# Revit family: KEUCO_34983010037
name_source: partatom
category: Allgemeines Modell
revit_build: Autodesk Revit 2016 (Build: 20150220_1215(x64)
units: mm (PartAtom-declared; Revit-internal decimal feet)

## family parameters
Arbeitsebenenbasiert = Ja
Beim Laden mit Abzugskörper schneiden = Nein
Bemaßung runder Anschluss = Durchmesser verwenden
Gemeinsam genutzt = Nein
Immer vertikal = Nein
Kann Basisbauteil für Bewehrung sein = Nein
Raumberechnungspunkt = Nein
Teiletyp = Normal

## types (6) — shared parameters
Beschreibung = zur Wandmontage
Softsitz nach oben klappbar
Gewicht = 0.522
Hersteller = KEUCO
Kategorie = ACC
Länge = 450 mm  [stored 1.47638 ft]
Serie = Plan
Tiefe = 537 mm  [stored 1.76181 ft]
URL = https://www.keuco.com
Verwendung = CA / DU
Vorgabe-Ansicht = 1219 mm

## per-type parameters (varying)
| type | Ausschreibungstext | Material Regal | Rahmen Material |
| 34983010037 | KEUCO PLAN CARE Klappsitz 34983010037
schwarzgrauer (RAL 7021) Klappsitz 
aus Polyurethan-Schaum, zur Wandmontage 
in ästhetischem, funktionalem Design, 
für sicheres Sitzen im Duschbereich,
Wandhalter und Sitzträger als Design-Element hochglanzverchromt,
antistatisch, leichte Reinigung ,
kann mit max. 60%-igen Ethanol- 
oder Propanol-Lösungen desinfiziert werden, 
andere Desinfektionsmittel empfehlen sich nicht,
nach oben klappbarer Sitz belastbar bis 150 kg,
Breite 450 mm, Länge der Sitzfläche 500 mm,
Ausladung 537 mm,
Der Sitz wird verdeckt angebracht 

Das Befestigungsmaterial ist separat zu bestellen!

Zur Montage (je nach Ankergrund/Mauerwerk) 
unbedingt erforderlich:
3 x Befestigungs-Set 3 (Artikel-Nr. 34992000100)
oder
3 x Befestigungs-Set 6 (Artikel-Nr. 34992000200)
oder
3 x Befestigungs-Set 9 (Artikel-Nr. 34995000200)
oder
3 x Befestigungs-Set 11 (Artikel-Nr. 34997000100) | Schwarzgrau | Stahl, verchromt |
| 34983010038 | KEUCO PLAN CARE Klappsitz 34983010038
lichtgrauer (RAL 7035) Klappsitz 
aus Polyurethan-Schaum, zur Wandmontage 
in ästhetischem, funktionalem Design, 
für sicheres Sitzen im Duschbereich,
Wandhalter und Sitzträger als Design-Element hochglanzverchromt,
antistatisch, leichte Reinigung ,
kann mit max. 60%-igen Ethanol- 
oder Propanol-Lösungen desinfiziert werden, 
andere Desinfektionsmittel empfehlen sich nicht,
nach oben klappbarer Sitz belastbar bis 150 kg,
Breite 450 mm, Länge der Sitzfläche 500 mm,
Ausladung 537 mm,
Der Sitz wird verdeckt angebracht 

Das Befestigungsmaterial ist separat zu bestellen!

Zur Montage (je nach Ankergrund/Mauerwerk) 
unbedingt erforderlich:
3 x Befestigungs-Set 3 (Artikel-Nr. 34992000100)
oder
3 x Befestigungs-Set 6 (Artikel-Nr. 34992000200)
oder
3 x Befestigungs-Set 9 (Artikel-Nr. 34995000200)
oder
3 x Befestigungs-Set 11 (Artikel-Nr. 34997000100) | Weiß (RAL 9010) | Stahl, verchromt |
| 34983010051 | KEUCO PLAN CARE Klappsitz 34983010051
weißer (RAL 9010) Klappsitz 
aus Polyurethan-Schaum, zur Wandmontage 
in ästhetischem, funktionalem Design, 
für sicheres Sitzen im Duschbereich,
Wandhalter und Sitzträger als Design-Element hochglanzverchromt,
antistatisch, leichte Reinigung ,
kann mit max. 60%-igen Ethanol- 
oder Propanol-Lösungen desinfiziert werden, 
andere Desinfektionsmittel empfehlen sich nicht,
nach oben klappbarer Sitz belastbar bis 150 kg,
Breite 450 mm, Länge der Sitzfläche 500 mm,
Ausladung 537 mm,
Der Sitz wird verdeckt angebracht 

Das Befestigungsmaterial ist separat zu bestellen!

Zur Montage (je nach Ankergrund/Mauerwerk) 
unbedingt erforderlich:
3 x Befestigungs-Set 3 (Artikel-Nr. 34992000100)
oder
3 x Befestigungs-Set 6 (Artikel-Nr. 34992000200)
oder
3 x Befestigungs-Set 9 (Artikel-Nr. 34995000200)
oder
3 x Befestigungs-Set 11 (Artikel-Nr. 34997000100) | Weiß (RAL 9010) | Stahl, verchromt |
| 34983170037 | KEUCO PLAN CARE Klappsitz 34983170037
schwarzgrauer (RAL 7021) Klappsitz 
aus Polyurethan-Schaum, zur Wandmontage 
in ästhetischem, funktionalem Design, 
für sicheres Sitzen im Duschbereich,
Wandhalter und Sitzträger als Design-Element 
aus lackiertem Aluminium,
antistatisch, leichte Reinigung ,
kann mit max. 60%-igen Ethanol- 
oder Propanol-Lösungen desinfiziert werden, 
andere Desinfektionsmittel empfehlen sich nicht,
nach oben klappbarer Sitz belastbar bis 150 kg,
Breite 450 mm, Länge der Sitzfläche 500 mm,
Ausladung 537 mm,
Der Sitz wird verdeckt angebracht 

Das Befestigungsmaterial ist separat zu bestellen!

Zur Montage (je nach Ankergrund/Mauerwerk) 
unbedingt erforderlich:
3 x Befestigungs-Set 3 (Artikel-Nr. 34992000100)
oder
3 x Befestigungs-Set 6 (Artikel-Nr. 34992000200)
oder
3 x Befestigungs-Set 9 (Artikel-Nr. 34995000200)
oder
3 x Befestigungs-Set 11 (Artikel-Nr. 34997000100) | Schwarzgrau | Aluminium 1100-H18 |
| 34983170038 | KEUCO PLAN CARE Klappsitz 34983170038
lichtgrauer (RAL 7035) Klappsitz 
aus Polyurethan-Schaum, zur Wandmontage 
in ästhetischem, funktionalem Design, 
für sicheres Sitzen im Duschbereich,
Wandhalter und Sitzträger als Design-Element 
aus lackiertem Aluminium,
antistatisch, leichte Reinigung ,
kann mit max. 60%-igen Ethanol- 
oder Propanol-Lösungen desinfiziert werden, 
andere Desinfektionsmittel empfehlen sich nicht,
nach oben klappbarer Sitz belastbar bis 150 kg,
Breite 450 mm, Länge der Sitzfläche 500 mm,
Ausladung 537 mm,
Der Sitz wird verdeckt angebracht 

Das Befestigungsmaterial ist separat zu bestellen!

Zur Montage (je nach Ankergrund/Mauerwerk) 
unbedingt erforderlich:
3 x Befestigungs-Set 3 (Artikel-Nr. 34992000100)
oder
3 x Befestigungs-Set 6 (Artikel-Nr. 34992000200)
oder
3 x Befestigungs-Set 9 (Artikel-Nr. 34995000200)
oder
3 x Befestigungs-Set 11 (Artikel-Nr. 34997000100) | Lichtgrau (RAL 7035) | Aluminium 1100-H18 |
| 34983170051 | KEUCO PLAN CARE Klappsitz 34983170051
weißer (RAL 9010) Klappsitz 
aus Polyurethan-Schaum, zur Wandmontage 
in ästhetischem, funktionalem Design, 
für sicheres Sitzen im Duschbereich,
Wandhalter und Sitzträger als Design-Element 
aus lackiertem Aluminium,
antistatisch, leichte Reinigung ,
kann mit max. 60%-igen Ethanol- 
oder Propanol-Lösungen desinfiziert werden, 
andere Desinfektionsmittel empfehlen sich nicht,
nach oben klappbarer Sitz belastbar bis 150 kg,
Breite 450 mm, Länge der Sitzfläche 500 mm,
Ausladung 537 mm,
Der Sitz wird verdeckt angebracht 

Das Befestigungsmaterial ist separat zu bestellen!

Zur Montage (je nach Ankergrund/Mauerwerk) 
unbedingt erforderlich:
3 x Befestigungs-Set 3 (Artikel-Nr. 34992000100)
oder
3 x Befestigungs-Set 6 (Artikel-Nr. 34992000200)
oder
3 x Befestigungs-Set 9 (Artikel-Nr. 34995000200)
oder
3 x Befestigungs-Set 11 (Artikel-Nr. 34997000100) | Lichtgrau (RAL 7035) | Aluminium 1100-H18 |

note: column(s) folded — value = type name in every type: Artikelnummer

note: [stored X ft] marks values corroborated as IEEE doubles in the binary element streams (Revit-internal decimal feet)

## geometry (parser evidence)
native form markers: Blend x2, Sweep x3
no freeform markers — native parametric forms only
